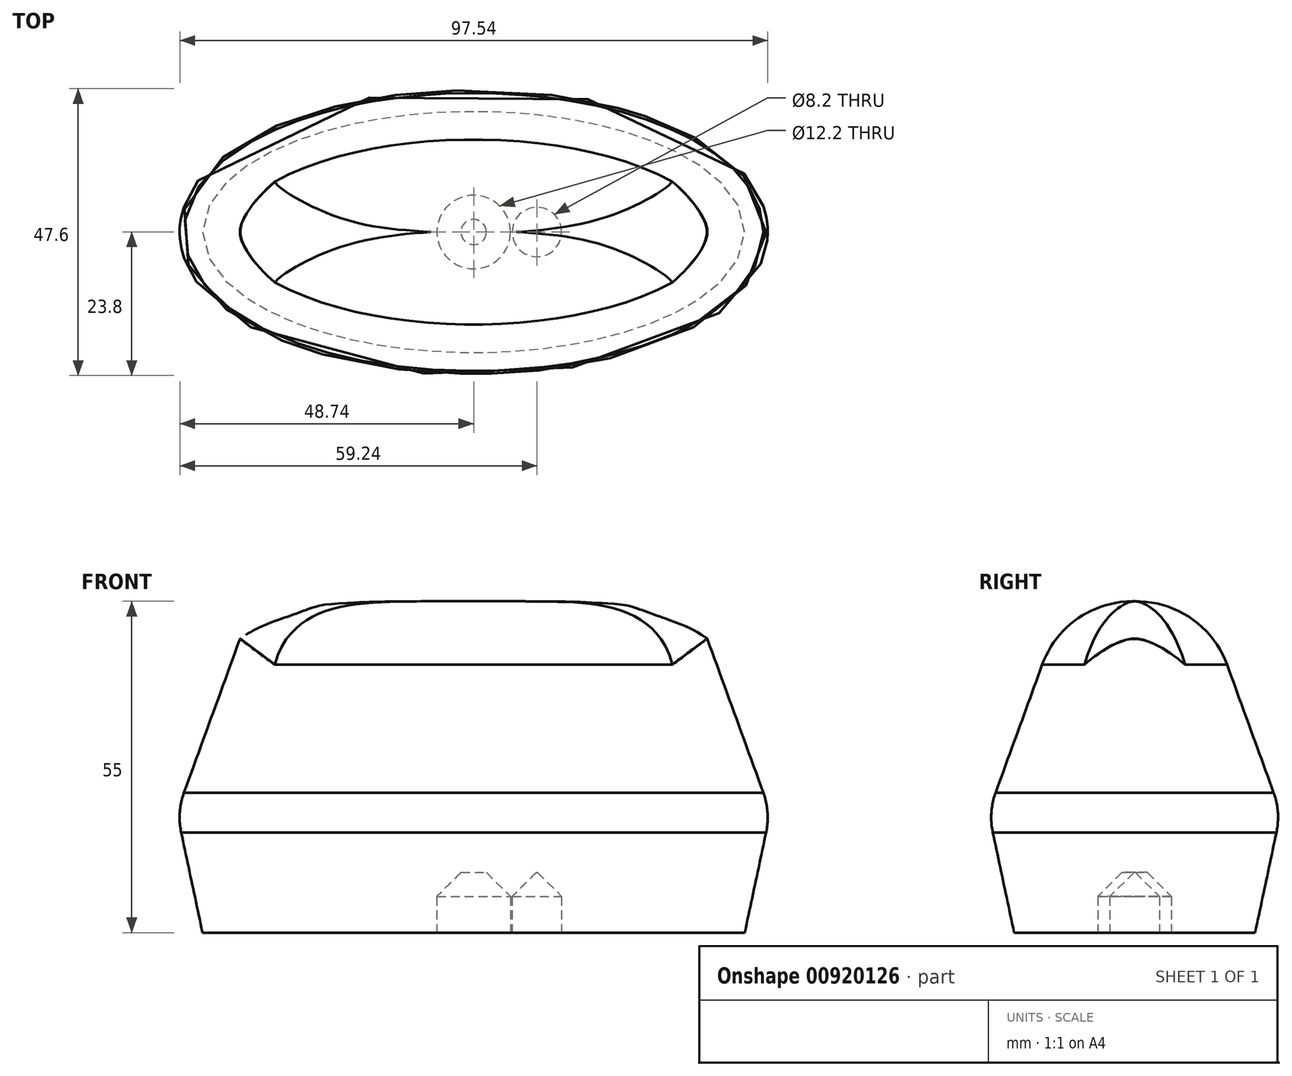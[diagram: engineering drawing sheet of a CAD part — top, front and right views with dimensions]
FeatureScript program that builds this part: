
annotation { "Feature Type Name" : "Feature", "Feature Type Description" : "" }
export const myFeature = defineFeature(function(context is Context, id is Id, definition is map)
    precondition{}
    {
        {
            var Q0;
            Q0=qCreatedBy(makeId("Top.planeOp"),FACE);
            var sketch = newSketch(context, id + "F0", { "sketchPlane" : qUnion([Q0])});
            skEllipse(sketch, "E0", {"center": v(0, 20) * mm, "majorRadius": 20 * mm, "minorRadius": 45 * mm, "majorAxis": v(0, -1)});
            skLineSegment(sketch, "E1", {"start": v(0, 0) * mm, "end": v(0, 40) * mm, "construction": true});
            skLineSegment(sketch, "E2", {"start": v(0, 20) * mm, "end": v(45, 20) * mm});
            skSolve(sketch);
        }
        {
            var Q0;
            Q0=makeQuery(id+"F0.imprint","IMPRINT",FACE,{"disambiguationData":[TD([[makeQuery(id+"F0.imprint","IMPRINT",EDGE,{"derivedFrom":sQuery(id+"F0.wireOp",EDGE,"E0")}),1.0]])]});
            extrude(context, id + "F1", {"entities" : qUnion([Q0]), "depth" : 20 * mm, "offsetDistance" : 25 * mm, "hasDraft" : true, "draftAngle" : 12 * degree});
        }
        {
            var Q0;
            Q0=makeQuery(id+"F1.opExtrude","CAP_FACE",FACE,{"disambiguationData":[OSD([sQuery(id+"F0.wireOp",EDGE,"E0")])],"isStart":false});
            extrude(context, id + "F2", {"entities" : qUnion([Q0]), "operationType" : NewBodyOperationType.ADD, "depth" : 35 * mm, "offsetDistance" : 25 * mm, "hasDraft" : true, "draftAngle" : 20 * degree, "draftPullDirection" : true});
        }
        {
            var Q0;
            Q0=makeQuery(id+"F2.opExtrude","CAP_FACE",FACE,{"disambiguationData":[OSD([sQuery(id+"F0.wireOp",EDGE,"E0")])],"isStart":false});
            fillet(context, id + "F3", {"entities" : qUnion([Q0]), "radius" : 16 * mm, "tangentPropagation" : true, "allowEdgeOverflow" : false});
        }
        {
            var Q0;
            {var subQ0=sQuery(id+"F0.wireOp",EDGE,"E0");Q0=makeQuery(id+"F2.boolean.opBoolean","MERGE",EDGE,{"derivedFrom":[makeQuery(id+"F1.opExtrude","CAP_EDGE",EDGE,{"disambiguationData":[OSD([subQ0])],"isStart":false}),makeQuery(id+"F2.opExtrude","CAP_EDGE",EDGE,{"disambiguationData":[OSD([subQ0])],"isStart":true})]});}
            fillet(context, id + "F4", {"entities" : qUnion([Q0]), "radius" : 12 * mm, "tangentPropagation" : true, "allowEdgeOverflow" : false});
        }
        {
            var Q0;
            Q0=makeQuery(id+"F1.opExtrude","CAP_FACE",FACE,{"disambiguationData":[OSD([sQuery(id+"F0.wireOp",EDGE,"E0")])],"isStart":true});
            var sketch = newSketch(context, id + "F5", { "sketchPlane" : qUnion([Q0])});
            skLineSegment(sketch, "E3", {"start": v(0, 0) * mm, "end": v(0, -40) * mm, "construction": true});
            skCircle(sketch, "E4", {"center": v(0, -20) * mm, "radius": 6.1 * mm});
            skCircle(sketch, "E5", {"center": v(10.5, -20) * mm, "radius": 4.1 * mm});
            skSolve(sketch);
        }
        {
            var Q0;
            Q0=makeQuery(id+"F5.imprint","IMPRINT",FACE,{"disambiguationData":[TD([[makeQuery(id+"F5.imprint","IMPRINT",EDGE,{"derivedFrom":sQuery(id+"F5.wireOp",EDGE,"E4")}),1.0]])]});
            var Q1;
            Q1=makeQuery(id+"F5.imprint","IMPRINT",FACE,{"disambiguationData":[TD([[makeQuery(id+"F5.imprint","IMPRINT",EDGE,{"derivedFrom":sQuery(id+"F5.wireOp",EDGE,"E5")}),1.0]])]});
            extrude(context, id + "F6", {"entities" : qUnion([Q0, Q1]), "operationType" : NewBodyOperationType.REMOVE, "oppositeDirection" : true, "depth" : 10 * mm, "offsetDistance" : 25 * mm});
        }
        {
            var Q0;
            Q0=makeQuery(id+"F6.boolean.opBoolean","COPY",FACE,{"derivedFrom":makeQuery(id+"F6.opExtrude","CAP_FACE",FACE,{"disambiguationData":[OSD([sQuery(id+"F5.wireOp",EDGE,"E4")])],"isStart":false})});
            var Q1;
            Q1=makeQuery(id+"F6.boolean.opBoolean","COPY",FACE,{"derivedFrom":makeQuery(id+"F6.opExtrude","CAP_FACE",FACE,{"disambiguationData":[OSD([sQuery(id+"F5.wireOp",EDGE,"E5")])],"isStart":false})});
            chamfer(context, id + "F7", {"entities" : qUnion([Q0, Q1]), "width" : 4 * mm, "tangentPropagation" : true});
        }
    });
